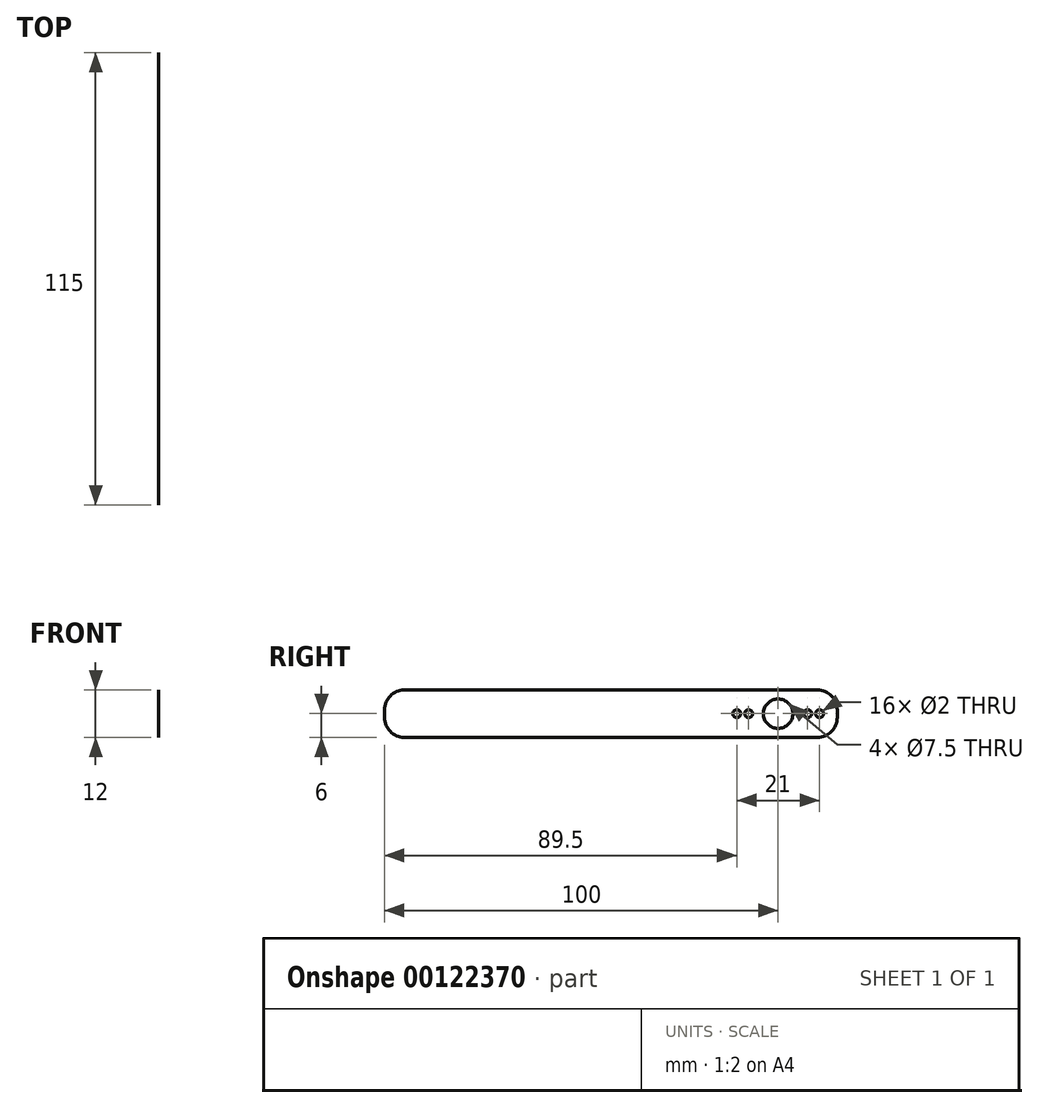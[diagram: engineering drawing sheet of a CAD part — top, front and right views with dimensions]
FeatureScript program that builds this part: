
annotation { "Feature Type Name" : "Feature", "Feature Type Description" : "" }
export const myFeature = defineFeature(function(context is Context, id is Id, definition is map)
    precondition{}
    {
        {
            var Q0;
            Q0=qCreatedBy(makeId("Right.planeOp"),FACE);
            var sketch = newSketch(context, id + "F0", { "sketchPlane" : qUnion([Q0])});
            skCircle(sketch, "E0", {"center": v(0, 0) * mm, "radius": 3.75 * mm});
            skCircle(sketch, "E1", {"center": v(-7.5, 0) * mm, "radius": 1 * mm});
            skCircle(sketch, "E2", {"center": v(7.5, 0) * mm, "radius": 1 * mm});
            skLineSegment(sketch, "E3.bottom", {"start": v(-100, 6) * mm, "end": v(15, 6) * mm});
            skLineSegment(sketch, "E3.top", {"start": v(-100, -6) * mm, "end": v(15, -6) * mm});
            skLineSegment(sketch, "E3.left", {"start": v(-100, 6) * mm, "end": v(-100, -6) * mm});
            skLineSegment(sketch, "E3.right", {"start": v(15, 6) * mm, "end": v(15, -6) * mm});
            skCircle(sketch, "E4", {"center": v(10.5, 0) * mm, "radius": 1 * mm});
            skCircle(sketch, "E5", {"center": v(-10.5, 0) * mm, "radius": 1 * mm});
            skSolve(sketch);
        }
        {
            var Q0;
            Q0=makeQuery(id+"F0.imprint","IMPRINT",FACE,{"disambiguationData":[TD([[makeQuery(id+"F0.imprint","IMPRINT",EDGE,{"derivedFrom":sQuery(id+"F0.wireOp",EDGE,"E0")}),-1.0]])]});
            extrude(context, id + "F1", {"entities" : qUnion([Q0]), "depth" : 1 / 203.2 * mm});
        }
        {
            var Q0;
            Q0=makeQuery(id+"F1.opExtrude","SWEPT_EDGE",EDGE,{"disambiguationData":[OSD([sQuery(id+"F0.wireOp",EDGE,"E3.bottom"),sQuery(id+"F0.wireOp",EDGE,"E3.left")])]});
            fillet(context, id + "F2", {"entities" : qUnion([Q0]), "radius" : 5 * mm, "tangentPropagation" : true, "allowEdgeOverflow" : false});
        }
        {
            var Q0;
            Q0=makeQuery(id+"F1.opExtrude","SWEPT_EDGE",EDGE,{"disambiguationData":[OSD([sQuery(id+"F0.wireOp",EDGE,"E3.top"),sQuery(id+"F0.wireOp",EDGE,"E3.left")])]});
            fillet(context, id + "F3", {"entities" : qUnion([Q0]), "radius" : 5 * mm, "tangentPropagation" : true, "allowEdgeOverflow" : false});
        }
        {
            var Q0;
            Q0=makeQuery(id+"F1.opExtrude","SWEPT_EDGE",EDGE,{"disambiguationData":[OSD([sQuery(id+"F0.wireOp",EDGE,"E3.bottom"),sQuery(id+"F0.wireOp",EDGE,"E3.right")])]});
            fillet(context, id + "F4", {"entities" : qUnion([Q0]), "radius" : 5 * mm, "tangentPropagation" : true, "allowEdgeOverflow" : false});
        }
        {
            var Q0;
            Q0=makeQuery(id+"F1.opExtrude","SWEPT_EDGE",EDGE,{"disambiguationData":[OSD([sQuery(id+"F0.wireOp",EDGE,"E3.top"),sQuery(id+"F0.wireOp",EDGE,"E3.right")])]});
            fillet(context, id + "F5", {"entities" : qUnion([Q0]), "radius" : 5 * mm, "tangentPropagation" : true, "allowEdgeOverflow" : false});
        }
    });
